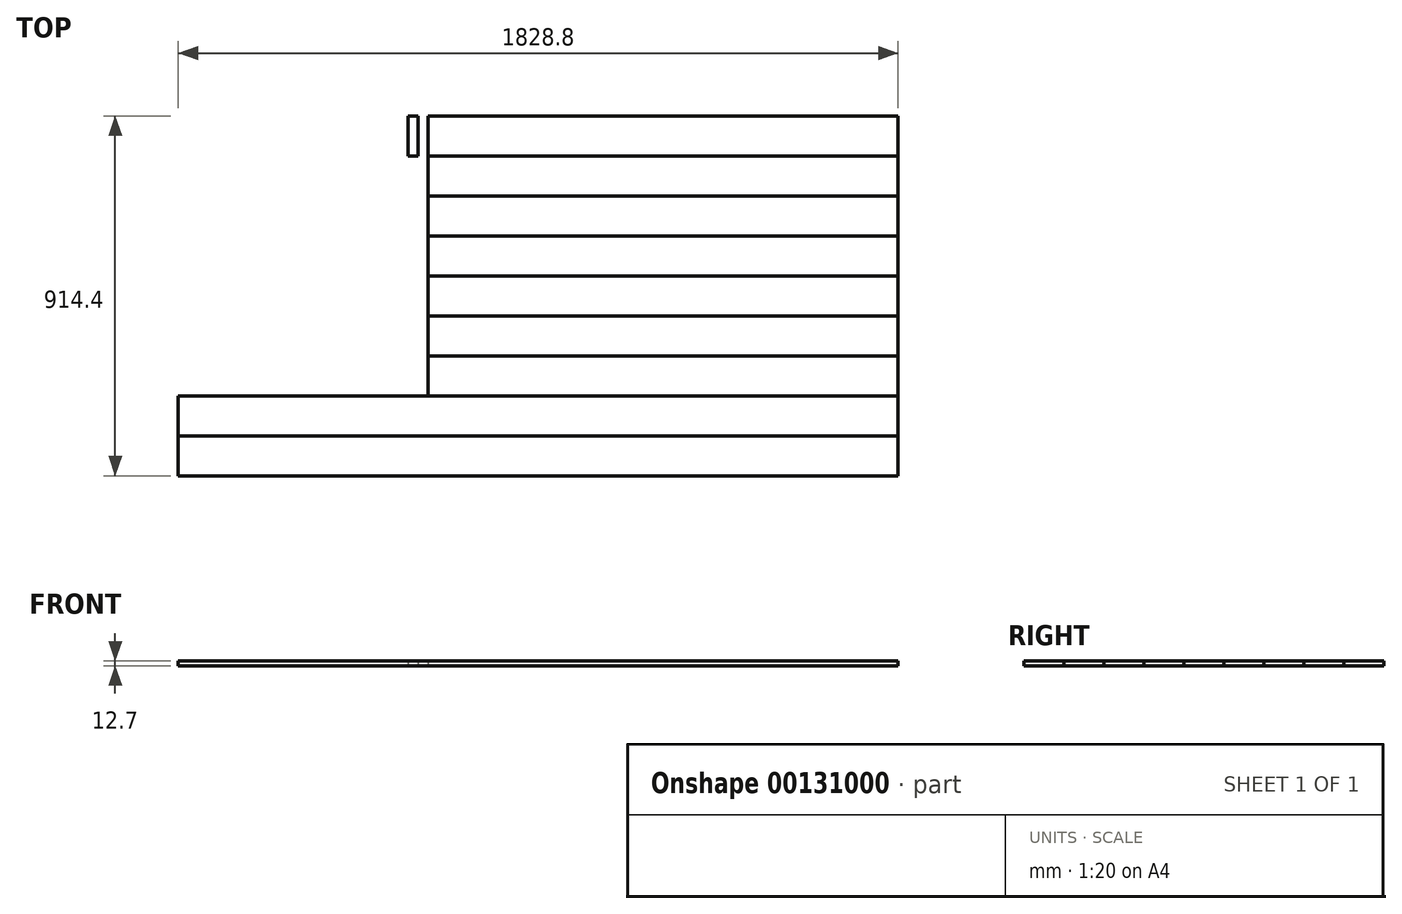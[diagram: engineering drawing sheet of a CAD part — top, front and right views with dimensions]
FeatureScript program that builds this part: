
annotation { "Feature Type Name" : "Feature", "Feature Type Description" : "" }
export const myFeature = defineFeature(function(context is Context, id is Id, definition is map)
    precondition{}
    {
        {
            var Q0;
            Q0=qCreatedBy(makeId("Top.planeOp"),FACE);
            var sketch = newSketch(context, id + "F0", { "sketchPlane" : qUnion([Q0])});
            skLineSegment(sketch, "E0.bottom", {"start": v(-1229.12, 406.4) * mm, "end": v(1209.28, 406.4) * mm});
            skLineSegment(sketch, "E0.top", {"start": v(-1229.12, -812.8) * mm, "end": v(1209.28, -812.8) * mm});
            skLineSegment(sketch, "E0.left", {"start": v(-1229.12, 406.4) * mm, "end": v(-1229.12, -812.8) * mm});
            skLineSegment(sketch, "E0.right", {"start": v(1209.28, 406.4) * mm, "end": v(1209.28, -812.8) * mm});
            skLineSegment(sketch, "E1", {"start": v(-1229.12, 304.8) * mm, "end": v(1209.28, 304.8) * mm});
            skLineSegment(sketch, "E2", {"start": v(-1229.12, 203.2) * mm, "end": v(1209.28, 203.2) * mm});
            skLineSegment(sketch, "E3", {"start": v(-1229.12, 101.6) * mm, "end": v(1209.28, 101.6) * mm});
            skLineSegment(sketch, "E4", {"start": v(-1229.12, 0) * mm, "end": v(1209.28, 0) * mm});
            skLineSegment(sketch, "E5", {"start": v(-1229.12, -203.2) * mm, "end": v(1209.28, -203.2) * mm});
            skLineSegment(sketch, "E6", {"start": v(-1229.12, -304.8) * mm, "end": v(1209.28, -304.8) * mm});
            skLineSegment(sketch, "E7", {"start": v(-1229.12, -101.6) * mm, "end": v(1209.28, -101.6) * mm});
            skPoint(sketch, "E7.endSnap0", {"position": v(1209.28, -203.2) * mm});
            skLineSegment(sketch, "E8", {"start": v(-619.52, -406.4) * mm, "end": v(1209.28, -406.4) * mm});
            skLineSegment(sketch, "E9", {"start": v(-1229.12, -508) * mm, "end": v(1209.28, -508) * mm});
            skLineSegment(sketch, "E10", {"start": v(-619.52, -304.8) * mm, "end": v(-619.52, -508) * mm});
            skPoint(sketch, "E11.orphan", {"position": v(-1229.12, -406.4) * mm});
            skLineSegment(sketch, "E12", {"start": v(-35.32, 406.4) * mm, "end": v(-35.32, -304.8) * mm});
            skLineSegment(sketch, "E13", {"start": v(15.48, 406.4) * mm, "end": v(15.48, -304.8) * mm});
            skPoint(sketch, "E14.orphan", {"position": v(-35.32, 406.1) * mm});
            skPoint(sketch, "E15.orphan", {"position": v(15.48, 406.4) * mm});
            skLineSegment(sketch, "E16", {"start": v(-9.92, 406.4) * mm, "end": v(-9.92, -304.8) * mm});
            skSolve(sketch);
        }
        {
            var Q0;
            {var subQ0=sQuery(id+"F0.wireOp",EDGE,"E0.right");var subQ1=sQuery(id+"F0.wireOp",EDGE,"E0.bottom");var subQ2=makeQuery(id+"F0.imprint","INTERSECT",VERTEX,{"derivedFrom":[subQ1,subQ0]});Q0=makeQuery(id+"F0.imprint","IMPRINT",FACE,{"disambiguationData":[TD([[makeQuery(id+"F0.imprint","IMPRINT",EDGE,{"disambiguationData":[TD([[subQ2,1.0]])],"derivedFrom":subQ1}),-1.0]])]});}
            extrude(context, id + "F1", {"entities" : qUnion([Q0]), "depth" : 12.7 * mm});
        }
        {
            var Q0;
            {var subQ0=sQuery(id+"F0.wireOp",EDGE,"E1");var subQ1=sQuery(id+"F0.wireOp",EDGE,"E0.right");var subQ2=makeQuery(id+"F0.imprint","INTERSECT",VERTEX,{"derivedFrom":[subQ1,subQ0]});Q0=makeQuery(id+"F0.imprint","IMPRINT",FACE,{"disambiguationData":[TD([[makeQuery(id+"F0.imprint","IMPRINT",EDGE,{"disambiguationData":[TD([[subQ2,-1.0]])],"derivedFrom":subQ1}),-1.0]])]});}
            extrude(context, id + "F2", {"entities" : qUnion([Q0]), "depth" : 12.7 * mm});
        }
        {
            var Q0;
            {var subQ0=sQuery(id+"F0.wireOp",EDGE,"E2");var subQ1=sQuery(id+"F0.wireOp",EDGE,"E0.right");var subQ2=makeQuery(id+"F0.imprint","INTERSECT",VERTEX,{"derivedFrom":[subQ1,subQ0]});Q0=makeQuery(id+"F0.imprint","IMPRINT",FACE,{"disambiguationData":[TD([[makeQuery(id+"F0.imprint","IMPRINT",EDGE,{"disambiguationData":[TD([[subQ2,-1.0]])],"derivedFrom":subQ1}),-1.0]])]});}
            extrude(context, id + "F3", {"entities" : qUnion([Q0]), "depth" : 12.7 * mm});
        }
        {
            var Q0;
            {var subQ0=sQuery(id+"F0.wireOp",EDGE,"E3");var subQ1=sQuery(id+"F0.wireOp",EDGE,"E0.right");var subQ2=makeQuery(id+"F0.imprint","INTERSECT",VERTEX,{"derivedFrom":[subQ1,subQ0]});Q0=makeQuery(id+"F0.imprint","IMPRINT",FACE,{"disambiguationData":[TD([[makeQuery(id+"F0.imprint","IMPRINT",EDGE,{"disambiguationData":[TD([[subQ2,-1.0]])],"derivedFrom":subQ1}),-1.0]])]});}
            extrude(context, id + "F4", {"entities" : qUnion([Q0]), "depth" : 12.7 * mm});
        }
        {
            var Q0;
            {var subQ0=sQuery(id+"F0.wireOp",EDGE,"E4");var subQ1=sQuery(id+"F0.wireOp",EDGE,"E0.right");var subQ2=makeQuery(id+"F0.imprint","INTERSECT",VERTEX,{"derivedFrom":[subQ1,subQ0]});Q0=makeQuery(id+"F0.imprint","IMPRINT",FACE,{"disambiguationData":[TD([[makeQuery(id+"F0.imprint","IMPRINT",EDGE,{"disambiguationData":[TD([[subQ2,-1.0]])],"derivedFrom":subQ1}),-1.0]])]});}
            extrude(context, id + "F5", {"entities" : qUnion([Q0]), "depth" : 12.7 * mm});
        }
        {
            var Q0;
            {var subQ0=sQuery(id+"F0.wireOp",EDGE,"E5");var subQ1=sQuery(id+"F0.wireOp",EDGE,"E0.right");var subQ2=makeQuery(id+"F0.imprint","INTERSECT",VERTEX,{"derivedFrom":[subQ1,subQ0]});Q0=makeQuery(id+"F0.imprint","IMPRINT",FACE,{"disambiguationData":[TD([[makeQuery(id+"F0.imprint","IMPRINT",EDGE,{"disambiguationData":[TD([[subQ2,1.0]])],"derivedFrom":subQ1}),-1.0]])]});}
            extrude(context, id + "F6", {"entities" : qUnion([Q0]), "depth" : 12.7 * mm});
        }
        {
            var Q0;
            {var subQ0=sQuery(id+"F0.wireOp",EDGE,"E5");var subQ1=sQuery(id+"F0.wireOp",EDGE,"E0.right");var subQ2=makeQuery(id+"F0.imprint","INTERSECT",VERTEX,{"derivedFrom":[subQ1,subQ0]});Q0=makeQuery(id+"F0.imprint","IMPRINT",FACE,{"disambiguationData":[TD([[makeQuery(id+"F0.imprint","IMPRINT",EDGE,{"disambiguationData":[TD([[subQ2,-1.0]])],"derivedFrom":subQ1}),-1.0]])]});}
            extrude(context, id + "F7", {"entities" : qUnion([Q0]), "depth" : 12.7 * mm});
        }
        {
            var Q0;
            {var subQ3=sQuery(id+"F0.wireOp",EDGE,"E8");Q0=makeQuery(id+"F0.imprint","IMPRINT",FACE,{"disambiguationData":[TD([[makeQuery(id+"F0.imprint","IMPRINT",EDGE,{"derivedFrom":subQ3}),1.0]])]});}
            extrude(context, id + "F8", {"entities" : qUnion([Q0]), "depth" : 12.7 * mm});
        }
        {
            var Q0;
            {var subQ0=sQuery(id+"F0.wireOp",EDGE,"E8");Q0=makeQuery(id+"F0.imprint","IMPRINT",FACE,{"disambiguationData":[TD([[makeQuery(id+"F0.imprint","IMPRINT",EDGE,{"derivedFrom":subQ0}),-1.0]])]});}
            extrude(context, id + "F9", {"entities" : qUnion([Q0]), "depth" : 12.7 * mm});
        }
        {
            var Q0;
            {var subQ0=sQuery(id+"F0.wireOp",EDGE,"E12");var subQ1=sQuery(id+"F0.wireOp",EDGE,"E0.bottom");var subQ2=makeQuery(id+"F0.imprint","INTERSECT",VERTEX,{"derivedFrom":[subQ1,subQ0]});Q0=makeQuery(id+"F0.imprint","IMPRINT",FACE,{"disambiguationData":[TD([[makeQuery(id+"F0.imprint","IMPRINT",EDGE,{"disambiguationData":[TD([[subQ2,-1.0]])],"derivedFrom":subQ1}),-1.0]])]});}
            extrude(context, id + "F10", {"entities" : qUnion([Q0]), "depth" : 12.7 * mm});
        }
    });
